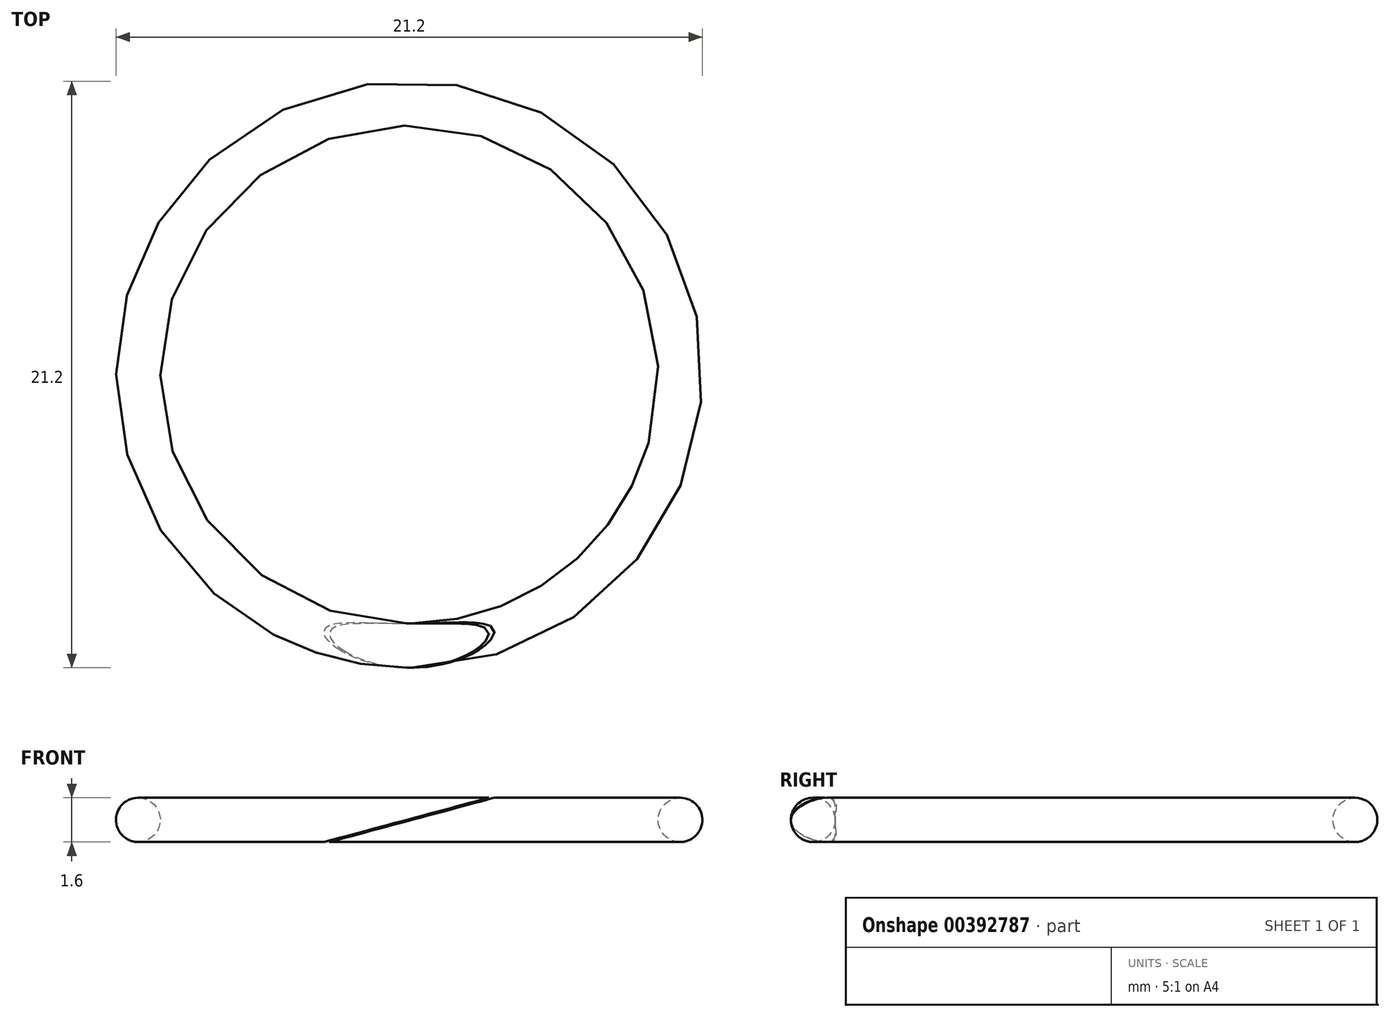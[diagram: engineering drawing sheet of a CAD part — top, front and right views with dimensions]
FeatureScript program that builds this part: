
annotation { "Feature Type Name" : "Feature", "Feature Type Description" : "" }
export const myFeature = defineFeature(function(context is Context, id is Id, definition is map)
    precondition{}
    {
        {
            assignVariable(context, id + "F0", {"name" : "ring_id", "anyValue" : 18});
        }
        {
            assignVariable(context, id + "F1", {"name" : "tube_diam", "anyValue" : 1.6});
        }
        {
            var Q0;
            Q0=qCreatedBy(makeId("Front.planeOp"),FACE);
            var sketch = newSketch(context, id + "F2", { "sketchPlane" : qUnion([Q0])});
            skCircle(sketch, "E0", {"center": v(9.8, 0) * mm, "radius": 0.8 * mm});
            skLineSegment(sketch, "E1", {"start": v(0, -4.73) * mm, "end": v(0, 9.22) * mm, "construction": true});
            skSolve(sketch);
        }
        {
            var Q0;
            Q0=qSketchRegion(id+"F2",true);
            var Q1;
            Q1=sQuery(id+"F2.wireOp",EDGE,"E1");
            revolve(context, id + "F3", {"entities" : qUnion([Q0]), "axis" : qUnion([Q1]), "revolveType" : RevolveType.FULL});
        }
        {
            var Q0;
            Q0=qCreatedBy(makeId("Front.planeOp"),FACE);
            var sketch = newSketch(context, id + "F4", { "sketchPlane" : qUnion([Q0])});
            skLineSegment(sketch, "E2", {"start": v(9.8, 0.8) * mm, "end": v(-9.8, 0.8) * mm, "construction": true});
            skLineSegment(sketch, "E3", {"start": v(9.8, -0.8) * mm, "end": v(-9.8, -0.8) * mm, "construction": true});
            skLineSegment(sketch, "E4", {"start": v(-3.09, 0.8) * mm, "end": v(-3.09, -0.8) * mm, "construction": true});
            skLineSegment(sketch, "E5", {"start": v(-3.09, -0.8) * mm, "end": v(2.89, 0.8) * mm});
            skLineSegment(sketch, "E6", {"start": v(3.09, 0.8) * mm, "end": v(-2.89, -0.8) * mm});
            skLineSegment(sketch, "E7", {"start": v(-3.09, -0.8) * mm, "end": v(-2.89, -0.8) * mm});
            skLineSegment(sketch, "E8", {"start": v(2.89, 0.8) * mm, "end": v(3.09, 0.8) * mm});
            skLineSegment(sketch, "E9", {"start": v(-0.1, 0) * mm, "end": v(0.1, 0) * mm});
            skSolve(sketch);
        }
        {
            var Q0;
            Q0=qSketchRegion(id+"F4",true);
            var Q1;
            Q1=makeQuery(id+"F3.opRevolve","SWEPT_BODY",BODY,{"disambiguationData":[OSD([sQuery(id+"F2.wireOp",EDGE,"E0")])]});
            extrude(context, id + "F5", {"entities" : qUnion([Q0]), "operationType" : NewBodyOperationType.REMOVE, "endBound" : BoundingType.THROUGH_ALL, "endBoundEntityBody" : qUnion([Q1]), "depth" : (getVariable(context, 'ring_id') + getVariable(context, 'tube_diam')) * mm});
        }
    });
